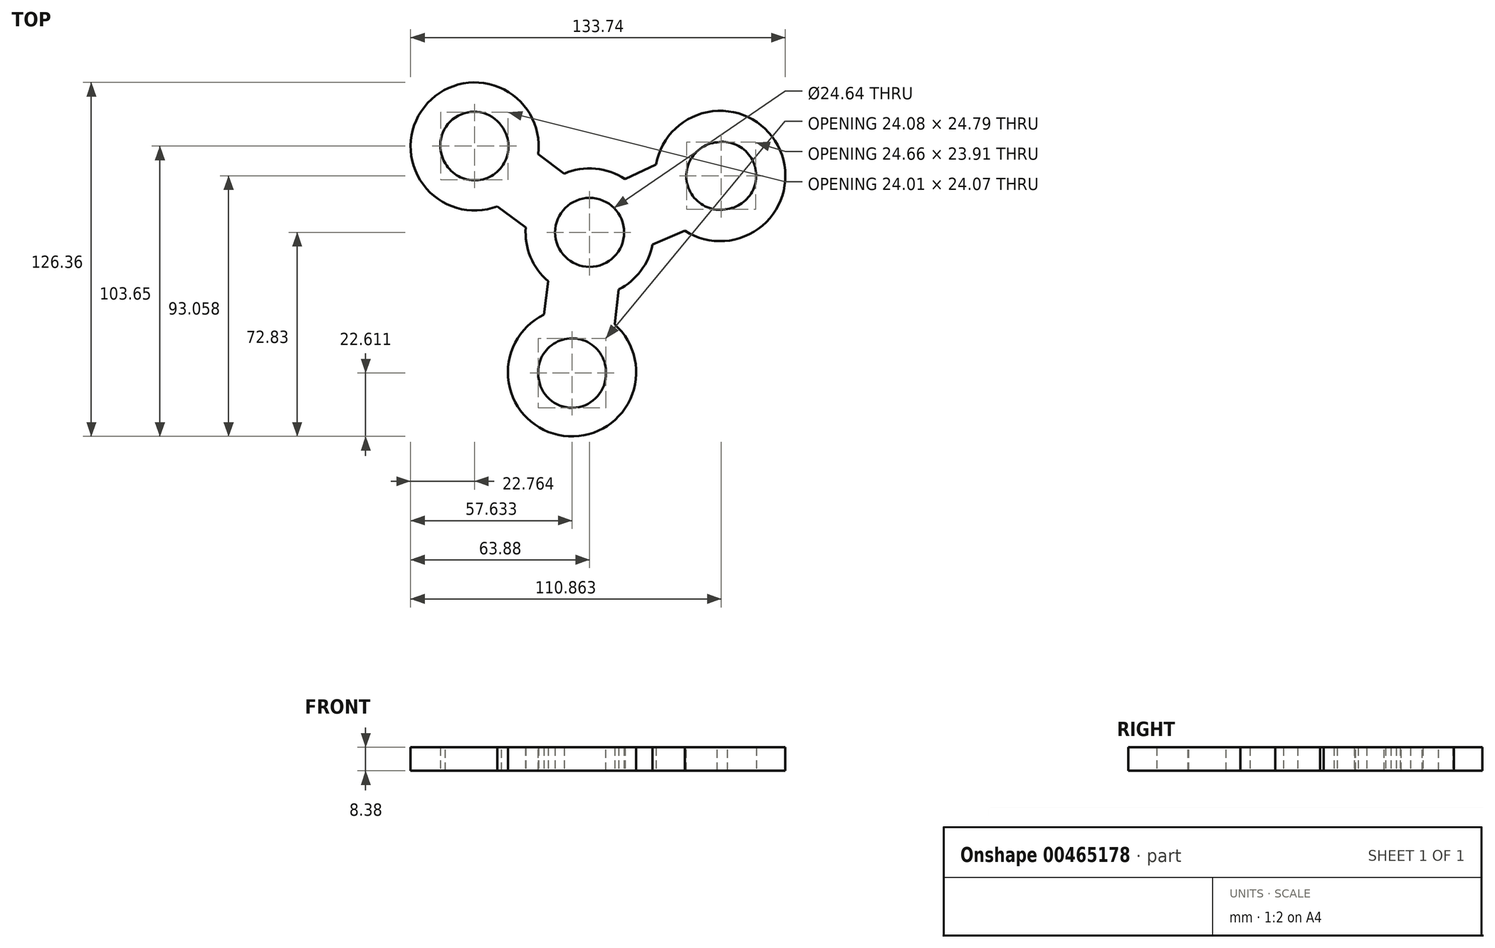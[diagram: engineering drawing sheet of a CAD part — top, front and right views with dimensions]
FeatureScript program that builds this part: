
annotation { "Feature Type Name" : "Feature", "Feature Type Description" : "" }
export const myFeature = defineFeature(function(context is Context, id is Id, definition is map)
    precondition{}
    {
        {
            var Q0;
            Q0=qCreatedBy(makeId("Top.planeOp"),FACE);
            var sketch = newSketch(context, id + "F0", { "sketchPlane" : qUnion([Q0])});
            skCircle(sketch, "E0", {"center": v(0, 0) * mm, "radius": 12.07 * mm});
            skSolve(sketch);
        }
        {
            var Q0;
            Q0=qCreatedBy(makeId("Top.planeOp"),FACE);
            var sketch = newSketch(context, id + "F1", { "sketchPlane" : qUnion([Q0])});
            skCircle(sketch, "E1", {"center": v(0, 0) * mm, "radius": 22.86 * mm});
            skSolve(sketch);
        }
        {
            var Q0;
            Q0=qCreatedBy(makeId("Top.planeOp"),FACE);
            var sketch = newSketch(context, id + "F2", { "sketchPlane" : qUnion([Q0])});
            skLineSegment(sketch, "E2", {"start": v(0, 0) * mm, "end": v(-40.71, 30.38) * mm});
            skLineSegment(sketch, "E3.1.0", {"start": v(0, 0) * mm, "end": v(-5.95, -50.45) * mm});
            skLineSegment(sketch, "E3.2.0", {"start": v(0, 0) * mm, "end": v(46.67, 20.07) * mm});
            skPoint(sketch, "E3.center", {"position": v(0, 0) * mm});
            skSolve(sketch);
        }
        {
            var Q0;
            Q0=qCreatedBy(makeId("Top.planeOp"),FACE);
            var sketch = newSketch(context, id + "F3", { "sketchPlane" : qUnion([Q0])});
            skCircle(sketch, "E4", {"center": v(-41.24, 31) * mm, "radius": 12.07 * mm});
            skCircle(sketch, "E5", {"center": v(47.4, 20.27) * mm, "radius": 12.07 * mm});
            skCircle(sketch, "E6", {"center": v(-6.26, -50.55) * mm, "radius": 12.07 * mm});
            skSolve(sketch);
        }
        {
            var Q0;
            Q0=qCreatedBy(makeId("Top.planeOp"),FACE);
            var sketch = newSketch(context, id + "F4", { "sketchPlane" : qUnion([Q0])});
            skLineSegment(sketch, "E7", {"start": v(0, 0) * mm, "end": v(-40.85, 30.7) * mm});
            skLineSegment(sketch, "E8", {"start": v(-40.85, 30.7) * mm, "end": v(-48.25, 20.84) * mm});
            skLineSegment(sketch, "E9", {"start": v(-48.25, 20.84) * mm, "end": v(-7.26, -9.96) * mm});
            skLineSegment(sketch, "E10", {"start": v(-7.26, -9.96) * mm, "end": v(0, 0) * mm});
            skLineSegment(sketch, "E11", {"start": v(0, 0) * mm, "end": v(6.68, 9.17) * mm});
            skLineSegment(sketch, "E12", {"start": v(6.68, 9.17) * mm, "end": v(-33.84, 39.61) * mm});
            skLineSegment(sketch, "E13", {"start": v(-33.84, 39.61) * mm, "end": v(-40.85, 30.7) * mm});
            skSolve(sketch);
        }
        {
            var Q0;
            Q0=qCreatedBy(makeId("Top.planeOp"),FACE);
            var sketch = newSketch(context, id + "F5", { "sketchPlane" : qUnion([Q0])});
            skCircle(sketch, "E14", {"center": v(-41.02, 30.67) * mm, "radius": 22.86 * mm});
            skCircle(sketch, "E15", {"center": v(46.6, 20.14) * mm, "radius": 23.26 * mm});
            skCircle(sketch, "E16", {"center": v(-6.26, -49.94) * mm, "radius": 22.89 * mm});
            skSolve(sketch);
        }
        {
            var Q0;
            Q0=qCreatedBy(makeId("Top.planeOp"),FACE);
            var sketch = newSketch(context, id + "F6", { "sketchPlane" : qUnion([Q0])});
            skLineSegment(sketch, "E17", {"start": v(0, 0) * mm, "end": v(-6.14, -50.8) * mm});
            skLineSegment(sketch, "E18", {"start": v(-6.14, -50.8) * mm, "end": v(-18.69, -49.28) * mm});
            skLineSegment(sketch, "E19", {"start": v(-18.69, -49.28) * mm, "end": v(-12.41, 2.7) * mm});
            skLineSegment(sketch, "E20", {"start": v(-12.41, 2.7) * mm, "end": v(0, 0) * mm});
            skLineSegment(sketch, "E21", {"start": v(0, 0) * mm, "end": v(12.7, -1.53) * mm});
            skLineSegment(sketch, "E22", {"start": v(12.7, -1.53) * mm, "end": v(6.56, -52.33) * mm});
            skLineSegment(sketch, "E23", {"start": v(6.56, -52.33) * mm, "end": v(-6.14, -50.8) * mm});
            skSolve(sketch);
        }
        {
            var Q0;
            Q0=qCreatedBy(makeId("Top.planeOp"),FACE);
            var sketch = newSketch(context, id + "F7", { "sketchPlane" : qUnion([Q0])});
            skLineSegment(sketch, "E24", {"start": v(0, 0) * mm, "end": v(46.78, 19.82) * mm});
            skLineSegment(sketch, "E25", {"start": v(46.78, 19.82) * mm, "end": v(41.4, 32.52) * mm});
            skLineSegment(sketch, "E26", {"start": v(46.78, 19.82) * mm, "end": v(51.73, 8.12) * mm});
            skLineSegment(sketch, "E27", {"start": v(0, 0) * mm, "end": v(-4.62, 10.9) * mm});
            skLineSegment(sketch, "E28", {"start": v(-4.62, 10.9) * mm, "end": v(0, 0) * mm});
            skLineSegment(sketch, "E29", {"start": v(41.4, 32.52) * mm, "end": v(-4.62, 10.9) * mm});
            skLineSegment(sketch, "E30", {"start": v(51.73, 8.12) * mm, "end": v(5.5, -11.46) * mm});
            skLineSegment(sketch, "E31", {"start": v(5.5, -11.46) * mm, "end": v(0, 0) * mm});
            skSolve(sketch);
        }
        {
            var Q0;
            Q0=makeQuery(id+"F1.imprint","IMPRINT",FACE,{"disambiguationData":[TD([[makeQuery(id+"F1.imprint","IMPRINT",EDGE,{"derivedFrom":sQuery(id+"F1.wireOp",EDGE,"E1")}),1.0]])]});
            var Q1;
            Q1=makeQuery(id+"F4.imprint","IMPRINT",FACE,{"disambiguationData":[TD([[makeQuery(id+"F4.imprint","IMPRINT",EDGE,{"derivedFrom":sQuery(id+"F4.wireOp",EDGE,"E7")}),1.0]])]});
            var Q2;
            Q2=makeQuery(id+"F4.imprint","IMPRINT",FACE,{"disambiguationData":[TD([[makeQuery(id+"F4.imprint","IMPRINT",EDGE,{"derivedFrom":sQuery(id+"F4.wireOp",EDGE,"E7")}),-1.0]])]});
            var Q3;
            Q3=makeQuery(id+"F5.imprint","IMPRINT",FACE,{"disambiguationData":[TD([[makeQuery(id+"F5.imprint","IMPRINT",EDGE,{"derivedFrom":sQuery(id+"F5.wireOp",EDGE,"E14")}),1.0]])]});
            var Q4;
            Q4=makeQuery(id+"F5.imprint","IMPRINT",FACE,{"disambiguationData":[TD([[makeQuery(id+"F5.imprint","IMPRINT",EDGE,{"derivedFrom":sQuery(id+"F5.wireOp",EDGE,"E15")}),1.0]])]});
            var Q5;
            Q5=makeQuery(id+"F5.imprint","IMPRINT",FACE,{"disambiguationData":[TD([[makeQuery(id+"F5.imprint","IMPRINT",EDGE,{"derivedFrom":sQuery(id+"F5.wireOp",EDGE,"E16")}),1.0]])]});
            var Q6;
            Q6=makeQuery(id+"F6.imprint","IMPRINT",FACE,{"disambiguationData":[TD([[makeQuery(id+"F6.imprint","IMPRINT",EDGE,{"derivedFrom":sQuery(id+"F6.wireOp",EDGE,"E17")}),-1.0]])]});
            var Q7;
            Q7=makeQuery(id+"F6.imprint","IMPRINT",FACE,{"disambiguationData":[TD([[makeQuery(id+"F6.imprint","IMPRINT",EDGE,{"derivedFrom":sQuery(id+"F6.wireOp",EDGE,"E17")}),1.0]])]});
            var Q8;
            Q8 = qSketchRegion(id + "F7", true);
            extrude(context, id + "F8", {"entities" : qUnion([Q0, Q1, Q2, Q3, Q4, Q5, Q6, Q7, Q8]), "depth" : 8.38 * mm});
        }
        {
            var Q0;
            Q0 = qSketchRegion(id + "F3", true);
            extrude(context, id + "F9", {"entities" : qUnion([Q0]), "operationType" : NewBodyOperationType.REMOVE, "depth" : 25.9 * mm});
        }
        {
            var Q0;
            Q0 = qSketchRegion(id + "F0", true);
            extrude(context, id + "F10", {"entities" : qUnion([Q0]), "operationType" : NewBodyOperationType.REMOVE, "depth" : 39.88 * mm});
        }
        {
            var Q0;
            Q0=makeQuery(id+"F8.opExtrude","SWEPT_BODY",BODY,{"disambiguationData":[OSD([sQuery(id+"F6.wireOp",EDGE,"E18"),sQuery(id+"F6.wireOp",EDGE,"E19"),sQuery(id+"F6.wireOp",EDGE,"E20"),sQuery(id+"F6.wireOp",EDGE,"E21"),sQuery(id+"F6.wireOp",EDGE,"E22"),sQuery(id+"F6.wireOp",EDGE,"E23")])]});
            var Q1;
            Q1=makeQuery(id+"F8.opExtrude","SWEPT_BODY",BODY,{"disambiguationData":[OSD([sQuery(id+"F4.wireOp",EDGE,"E8"),sQuery(id+"F4.wireOp",EDGE,"E9"),sQuery(id+"F4.wireOp",EDGE,"E10"),sQuery(id+"F4.wireOp",EDGE,"E11"),sQuery(id+"F4.wireOp",EDGE,"E12"),sQuery(id+"F4.wireOp",EDGE,"E13")])]});
            var Q2;
            Q2=makeQuery(id+"F8.opExtrude","SWEPT_BODY",BODY,{"disambiguationData":[OSD([sQuery(id+"F5.wireOp",EDGE,"E14")])]});
            var Q3;
            Q3=makeQuery(id+"F8.opExtrude","SWEPT_BODY",BODY,{"disambiguationData":[OSD([sQuery(id+"F1.wireOp",EDGE,"E1")])]});
            var Q4;
            Q4=makeQuery(id+"F8.opExtrude","SWEPT_BODY",BODY,{"disambiguationData":[OSD([sQuery(id+"F5.wireOp",EDGE,"E15")])]});
            var Q5;
            Q5=makeQuery(id+"F8.opExtrude","SWEPT_BODY",BODY,{"disambiguationData":[OSD([sQuery(id+"F5.wireOp",EDGE,"E16")])]});
            var Q6;
            Q6=makeQuery(id+"F8.opExtrude","SWEPT_BODY",BODY,{"disambiguationData":[OSD([sQuery(id+"F7.wireOp",EDGE,"E25"),sQuery(id+"F7.wireOp",EDGE,"E26"),sQuery(id+"F7.wireOp",EDGE,"E28"),sQuery(id+"F7.wireOp",EDGE,"E29"),sQuery(id+"F7.wireOp",EDGE,"E30"),sQuery(id+"F7.wireOp",EDGE,"E31")])]});
            booleanBodies(context, id + "F11", {"operationType" : BooleanOperationType.UNION, "tools" : qUnion([Q0, Q1, Q2, Q3, Q4, Q5, Q6])});
        }
        {
            var Q0;
            Q0=makeQuery(id+"F11.opBoolean","MERGE",FACE,{"derivedFrom":[makeQuery(id+"F8.opExtrude","CAP_FACE",FACE,{"disambiguationData":[OSD([sQuery(id+"F1.wireOp",EDGE,"E1")])],"isStart":false}),makeQuery(id+"F8.opExtrude","CAP_FACE",FACE,{"disambiguationData":[OSD([sQuery(id+"F4.wireOp",EDGE,"E8"),sQuery(id+"F4.wireOp",EDGE,"E9"),sQuery(id+"F4.wireOp",EDGE,"E10"),sQuery(id+"F4.wireOp",EDGE,"E11"),sQuery(id+"F4.wireOp",EDGE,"E12"),sQuery(id+"F4.wireOp",EDGE,"E13")])],"isStart":false}),makeQuery(id+"F8.opExtrude","CAP_FACE",FACE,{"disambiguationData":[OSD([sQuery(id+"F5.wireOp",EDGE,"E14")])],"isStart":false}),makeQuery(id+"F8.opExtrude","CAP_FACE",FACE,{"disambiguationData":[OSD([sQuery(id+"F5.wireOp",EDGE,"E15")])],"isStart":false}),makeQuery(id+"F8.opExtrude","CAP_FACE",FACE,{"disambiguationData":[OSD([sQuery(id+"F5.wireOp",EDGE,"E16")])],"isStart":false}),makeQuery(id+"F8.opExtrude","CAP_FACE",FACE,{"disambiguationData":[OSD([sQuery(id+"F6.wireOp",EDGE,"E18"),sQuery(id+"F6.wireOp",EDGE,"E19"),sQuery(id+"F6.wireOp",EDGE,"E20"),sQuery(id+"F6.wireOp",EDGE,"E21"),sQuery(id+"F6.wireOp",EDGE,"E22"),sQuery(id+"F6.wireOp",EDGE,"E23")])],"isStart":false}),makeQuery(id+"F8.opExtrude","CAP_FACE",FACE,{"disambiguationData":[OSD([sQuery(id+"F7.wireOp",EDGE,"E25"),sQuery(id+"F7.wireOp",EDGE,"E26"),sQuery(id+"F7.wireOp",EDGE,"E28"),sQuery(id+"F7.wireOp",EDGE,"E29"),sQuery(id+"F7.wireOp",EDGE,"E30"),sQuery(id+"F7.wireOp",EDGE,"E31")])],"isStart":false})]});
            var sketch = newSketch(context, id + "F12", { "sketchPlane" : qUnion([Q0])});
            skCircle(sketch, "E32", {"center": v(-41.02, 30.67) * mm, "radius": 12.08 * mm});
            skCircle(sketch, "E33", {"center": v(-6.26, -49.94) * mm, "radius": 12.12 * mm});
            skCircle(sketch, "E34", {"center": v(46.6, 20.14) * mm, "radius": 12.09 * mm});
            skSolve(sketch);
        }
        {
            var Q0;
            Q0 = qSketchRegion(id + "F12", true);
            extrude(context, id + "F13", {"entities" : qUnion([Q0]), "operationType" : NewBodyOperationType.REMOVE, "oppositeDirection" : true, "depth" : 25.4 * mm});
        }
        {
            var Q0;
            Q0=makeQuery(id+"F11.opBoolean","MERGE",FACE,{"derivedFrom":[makeQuery(id+"F8.opExtrude","CAP_FACE",FACE,{"disambiguationData":[OSD([sQuery(id+"F1.wireOp",EDGE,"E1")])],"isStart":true}),makeQuery(id+"F8.opExtrude","CAP_FACE",FACE,{"disambiguationData":[OSD([sQuery(id+"F4.wireOp",EDGE,"E8"),sQuery(id+"F4.wireOp",EDGE,"E9"),sQuery(id+"F4.wireOp",EDGE,"E10"),sQuery(id+"F4.wireOp",EDGE,"E11"),sQuery(id+"F4.wireOp",EDGE,"E12"),sQuery(id+"F4.wireOp",EDGE,"E13")])],"isStart":true}),makeQuery(id+"F8.opExtrude","CAP_FACE",FACE,{"disambiguationData":[OSD([sQuery(id+"F5.wireOp",EDGE,"E14")])],"isStart":true}),makeQuery(id+"F8.opExtrude","CAP_FACE",FACE,{"disambiguationData":[OSD([sQuery(id+"F5.wireOp",EDGE,"E15")])],"isStart":true}),makeQuery(id+"F8.opExtrude","CAP_FACE",FACE,{"disambiguationData":[OSD([sQuery(id+"F5.wireOp",EDGE,"E16")])],"isStart":true}),makeQuery(id+"F8.opExtrude","CAP_FACE",FACE,{"disambiguationData":[OSD([sQuery(id+"F6.wireOp",EDGE,"E18"),sQuery(id+"F6.wireOp",EDGE,"E19"),sQuery(id+"F6.wireOp",EDGE,"E20"),sQuery(id+"F6.wireOp",EDGE,"E21"),sQuery(id+"F6.wireOp",EDGE,"E22"),sQuery(id+"F6.wireOp",EDGE,"E23")])],"isStart":true}),makeQuery(id+"F8.opExtrude","CAP_FACE",FACE,{"disambiguationData":[OSD([sQuery(id+"F7.wireOp",EDGE,"E25"),sQuery(id+"F7.wireOp",EDGE,"E26"),sQuery(id+"F7.wireOp",EDGE,"E28"),sQuery(id+"F7.wireOp",EDGE,"E29"),sQuery(id+"F7.wireOp",EDGE,"E30"),sQuery(id+"F7.wireOp",EDGE,"E31")])],"isStart":true})]});
            var sketch = newSketch(context, id + "F14", { "sketchPlane" : qUnion([Q0])});
            skCircle(sketch, "E35", {"center": v(0, 0) * mm, "radius": 12.32 * mm});
            skSolve(sketch);
        }
        {
            var Q0;
            Q0 = qSketchRegion(id + "F14", true);
            extrude(context, id + "F15", {"entities" : qUnion([Q0]), "operationType" : NewBodyOperationType.REMOVE, "oppositeDirection" : true, "depth" : 25.4 * mm});
        }
    });
